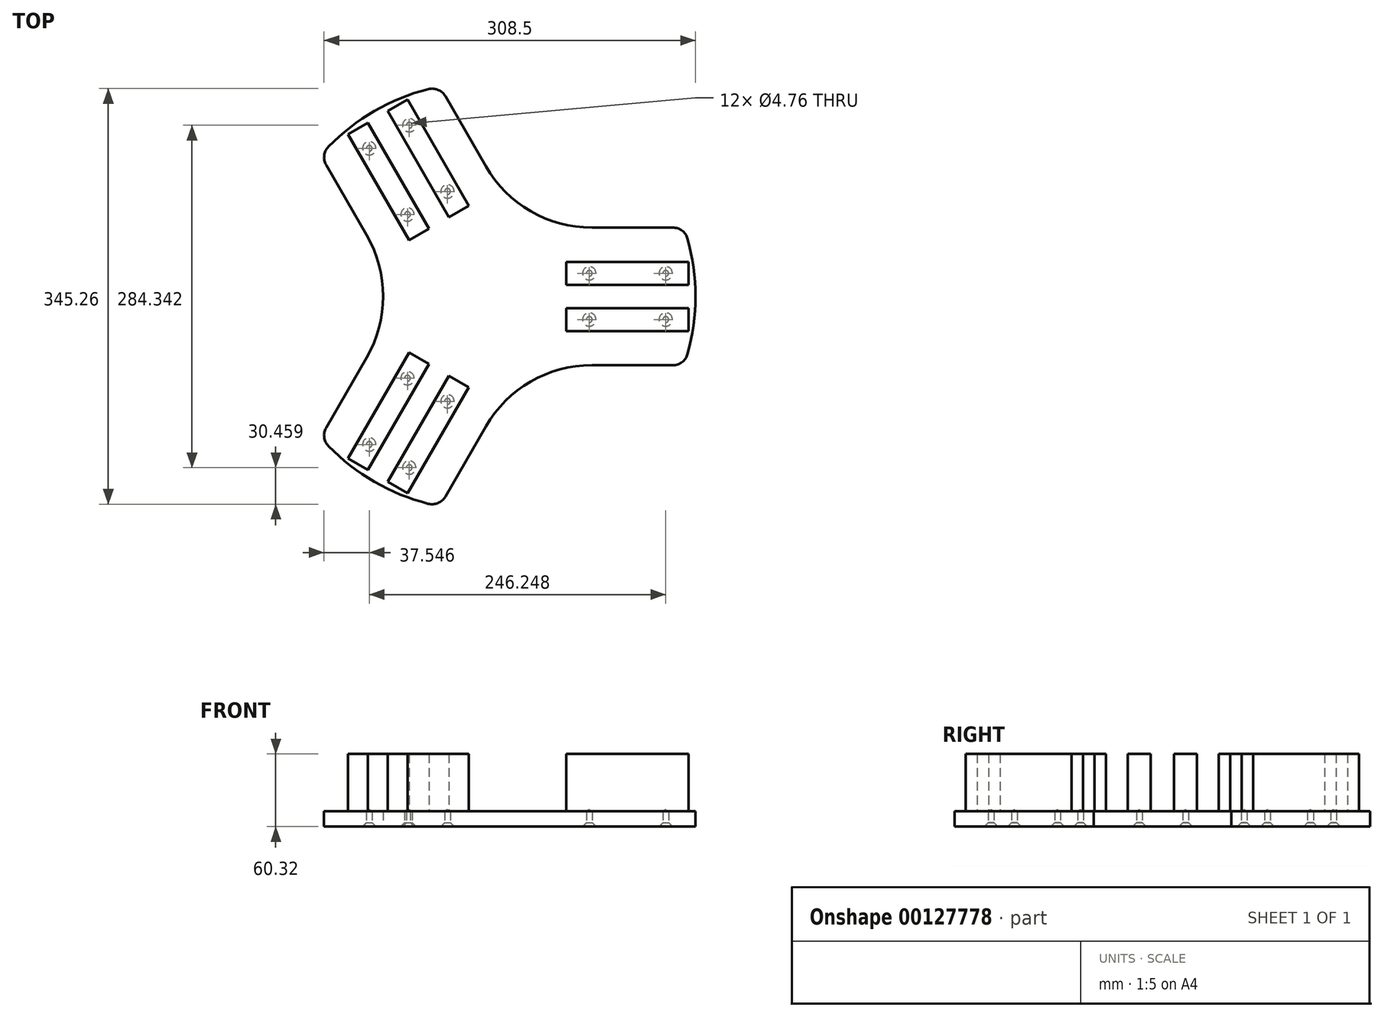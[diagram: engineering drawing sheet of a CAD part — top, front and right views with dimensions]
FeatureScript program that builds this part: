
annotation { "Feature Type Name" : "Feature", "Feature Type Description" : "" }
export const myFeature = defineFeature(function(context is Context, id is Id, definition is map)
    precondition{}
    {
        {
            var Q0;
            Q0=qCreatedBy(makeId("Top.planeOp"),FACE);
            var sketch = newSketch(context, id + "F0", { "sketchPlane" : qUnion([Q0])});
            skArc(sketch, "E0", {"start": v(171.23, -47.87) * mm, "mid": v(177.8, 0) * mm, "end": v(171.23, 47.87) * mm});
            skLineSegment(sketch, "E1", {"start": v(0, 0) * mm, "end": v(177.8, 0) * mm});
            skLineSegment(sketch, "E2", {"start": v(172.14, 9.65) * mm, "end": v(172.14, 28.7) * mm});
            skLineSegment(sketch, "E3.0", {"start": v(70.54, 9.65) * mm, "end": v(70.54, 28.7) * mm});
            skLineSegment(sketch, "E4", {"start": v(70.54, 28.7) * mm, "end": v(172.14, 28.7) * mm});
            skLineSegment(sketch, "E5", {"start": v(172.14, 9.65) * mm, "end": v(70.54, 9.65) * mm});
            skLineSegment(sketch, "E6.MirrorCS", {"start": v(172.14, -9.65) * mm, "end": v(172.14, -28.7) * mm});
            skLineSegment(sketch, "E7.MirrorCS", {"start": v(172.14, -9.65) * mm, "end": v(70.54, -9.65) * mm});
            skLineSegment(sketch, "E8.MirrorCS", {"start": v(70.54, -9.65) * mm, "end": v(70.54, -28.7) * mm});
            skLineSegment(sketch, "E9.MirrorCS", {"start": v(70.54, -28.7) * mm, "end": v(172.14, -28.7) * mm});
            skLineSegment(sketch, "E10.1.0", {"start": v(-60.13, 46.74) * mm, "end": v(-110.93, 134.73) * mm});
            skLineSegment(sketch, "E10.1.1", {"start": v(0, 0) * mm, "end": v(-88.9, 153.98) * mm});
            skLineSegment(sketch, "E10.1.2", {"start": v(-26.91, 65.92) * mm, "end": v(-10.41, 75.44) * mm});
            skLineSegment(sketch, "E10.1.3", {"start": v(-43.63, 56.27) * mm, "end": v(-60.13, 46.74) * mm});
            skLineSegment(sketch, "E10.1.4", {"start": v(-94.43, 144.25) * mm, "end": v(-110.93, 134.73) * mm});
            skLineSegment(sketch, "E10.1.5", {"start": v(-10.41, 75.44) * mm, "end": v(-61.21, 163.43) * mm});
            skLineSegment(sketch, "E10.1.6", {"start": v(-77.71, 153.9) * mm, "end": v(-61.21, 163.43) * mm});
            skLineSegment(sketch, "E10.1.7", {"start": v(-77.71, 153.9) * mm, "end": v(-26.91, 65.92) * mm});
            skLineSegment(sketch, "E10.1.8", {"start": v(-94.43, 144.25) * mm, "end": v(-43.63, 56.27) * mm});
            skLineSegment(sketch, "E10.2.0", {"start": v(-10.41, -75.44) * mm, "end": v(-61.21, -163.43) * mm});
            skLineSegment(sketch, "E10.2.1", {"start": v(0, 0) * mm, "end": v(-88.9, -153.98) * mm});
            skLineSegment(sketch, "E10.2.2", {"start": v(-43.63, -56.27) * mm, "end": v(-60.13, -46.74) * mm});
            skLineSegment(sketch, "E10.2.3", {"start": v(-26.91, -65.92) * mm, "end": v(-10.41, -75.44) * mm});
            skLineSegment(sketch, "E10.2.4", {"start": v(-77.71, -153.9) * mm, "end": v(-61.21, -163.43) * mm});
            skLineSegment(sketch, "E10.2.5", {"start": v(-60.13, -46.74) * mm, "end": v(-110.93, -134.73) * mm});
            skLineSegment(sketch, "E10.2.6", {"start": v(-94.43, -144.25) * mm, "end": v(-110.93, -134.73) * mm});
            skLineSegment(sketch, "E10.2.7", {"start": v(-94.43, -144.25) * mm, "end": v(-43.63, -56.27) * mm});
            skLineSegment(sketch, "E10.2.8", {"start": v(-77.71, -153.9) * mm, "end": v(-26.91, -65.92) * mm});
            skLineSegment(sketch, "E11.0", {"start": v(91.65, -57.15) * mm, "end": v(159, -57.15) * mm});
            skLineSegment(sketch, "E12.0", {"start": v(3.67, -107.95) * mm, "end": v(-30, -166.28) * mm});
            skArc(sketch, "E13.filletArc", {"start": v(91.65, -57.15) * mm, "mid": v(40.85, -70.76) * mm, "end": v(3.67, -107.95) * mm});
            skLineSegment(sketch, "E14.1.0", {"start": v(3.67, 107.95) * mm, "end": v(-30, 166.28) * mm});
            skArc(sketch, "E14.1.1", {"start": v(3.67, 107.95) * mm, "mid": v(40.85, 70.76) * mm, "end": v(91.65, 57.15) * mm});
            skLineSegment(sketch, "E14.1.2", {"start": v(91.65, 57.15) * mm, "end": v(159, 57.15) * mm});
            skLineSegment(sketch, "E14.2.0", {"start": v(-95.32, -50.8) * mm, "end": v(-129, -109.13) * mm});
            skArc(sketch, "E14.2.1", {"start": v(-95.32, -50.8) * mm, "mid": v(-81.7, 0) * mm, "end": v(-95.32, 50.8) * mm});
            skLineSegment(sketch, "E14.2.2", {"start": v(-95.32, 50.8) * mm, "end": v(-129, 109.13) * mm});
            skArc(sketch, "E15.trimOffspring", {"start": v(-44.16, 172.23) * mm, "mid": v(-88.9, 153.98) * mm, "end": v(-127.07, 124.36) * mm});
            skArc(sketch, "E16.trimOffspring", {"start": v(-127.07, -124.36) * mm, "mid": v(-88.9, -153.98) * mm, "end": v(-44.16, -172.23) * mm});
            skPoint(sketch, "E17.visualSharp", {"position": v(-133.68, 117.23) * mm});
            skArc(sketch, "E17.filletArc", {"start": v(-127.07, 124.36) * mm, "mid": v(-130.6, 117.07) * mm, "end": v(-129, 109.13) * mm});
            skPoint(sketch, "E18.visualSharp", {"position": v(-34.69, 174.38) * mm});
            skArc(sketch, "E18.filletArc", {"start": v(-30, 166.28) * mm, "mid": v(-36.08, 171.63) * mm, "end": v(-44.16, 172.23) * mm});
            skPoint(sketch, "E19.visualSharp", {"position": v(168.36, 57.15) * mm});
            skArc(sketch, "E19.filletArc", {"start": v(171.23, 47.87) * mm, "mid": v(166.68, 54.57) * mm, "end": v(159, 57.15) * mm});
            skPoint(sketch, "E20.visualSharp", {"position": v(168.36, -57.15) * mm});
            skArc(sketch, "E20.filletArc", {"start": v(159, -57.15) * mm, "mid": v(166.68, -54.57) * mm, "end": v(171.23, -47.87) * mm});
            skPoint(sketch, "E21.visualSharp", {"position": v(-34.69, -174.38) * mm});
            skArc(sketch, "E21.filletArc", {"start": v(-44.16, -172.23) * mm, "mid": v(-36.08, -171.63) * mm, "end": v(-30, -166.28) * mm});
            skPoint(sketch, "E22.visualSharp", {"position": v(-133.68, -117.23) * mm});
            skArc(sketch, "E22.filletArc", {"start": v(-129, -109.13) * mm, "mid": v(-130.6, -117.07) * mm, "end": v(-127.07, -124.36) * mm});
            skPoint(sketch, "E23", {"position": v(-93.15, -123) * mm});
            skPoint(sketch, "E24", {"position": v(-61.4, -68) * mm});
            skPoint(sketch, "E25", {"position": v(-28.19, -87.18) * mm});
            skPoint(sketch, "E26", {"position": v(-59.94, -142.17) * mm});
            skPoint(sketch, "E27.1.0", {"position": v(153.1, -19.18) * mm});
            skPoint(sketch, "E27.1.1", {"position": v(89.6, -19.18) * mm});
            skPoint(sketch, "E27.1.2", {"position": v(89.6, 19.18) * mm});
            skPoint(sketch, "E27.1.3", {"position": v(153.1, 19.18) * mm});
            skPoint(sketch, "E27.2.0", {"position": v(-59.94, 142.17) * mm});
            skPoint(sketch, "E27.2.1", {"position": v(-28.19, 87.18) * mm});
            skPoint(sketch, "E27.2.2", {"position": v(-61.4, 68) * mm});
            skPoint(sketch, "E27.2.3", {"position": v(-93.15, 123) * mm});
            skSolve(sketch);
        }
        {
            var Q0;
            Q0=makeQuery(id+"F0.imprint","IMPRINT",FACE,{"disambiguationData":[TD([[makeQuery(id+"F0.imprint","IMPRINT",EDGE,{"derivedFrom":sQuery(id+"F0.wireOp",EDGE,"E10.1.0")}),1.0]])]});
            var Q1;
            {var subQ3=sQuery(id+"F0.wireOp",EDGE,"E1");Q1=makeQuery(id+"F0.imprint","IMPRINT",FACE,{"disambiguationData":[TD([[makeQuery(id+"F0.imprint","IMPRINT",EDGE,{"derivedFrom":subQ3}),1.0]])]});}
            var Q2;
            {var subQ2=sQuery(id+"F0.wireOp",EDGE,"E1");Q2=makeQuery(id+"F0.imprint","IMPRINT",FACE,{"disambiguationData":[TD([[makeQuery(id+"F0.imprint","IMPRINT",EDGE,{"derivedFrom":subQ2}),-1.0]])]});}
            extrude(context, id + "F1", {"entities" : qUnion([Q0, Q1, Q2]), "depth" : 12.7 * mm});
        }
        {
            var Q0;
            Q0=makeQuery(id+"F0.imprint","IMPRINT",FACE,{"disambiguationData":[TD([[makeQuery(id+"F0.imprint","IMPRINT",EDGE,{"derivedFrom":sQuery(id+"F0.wireOp",EDGE,"E10.2.2")}),1.0]])]});
            var Q1;
            Q1=makeQuery(id+"F0.imprint","IMPRINT",FACE,{"disambiguationData":[TD([[makeQuery(id+"F0.imprint","IMPRINT",EDGE,{"derivedFrom":sQuery(id+"F0.wireOp",EDGE,"E10.2.0")}),-1.0]])]});
            var Q2;
            Q2=makeQuery(id+"F0.imprint","IMPRINT",FACE,{"disambiguationData":[TD([[makeQuery(id+"F0.imprint","IMPRINT",EDGE,{"derivedFrom":sQuery(id+"F0.wireOp",EDGE,"E6.MirrorCS")}),-1.0]])]});
            var Q3;
            Q3=makeQuery(id+"F0.imprint","IMPRINT",FACE,{"disambiguationData":[TD([[makeQuery(id+"F0.imprint","IMPRINT",EDGE,{"derivedFrom":sQuery(id+"F0.wireOp",EDGE,"E2")}),1.0]])]});
            var Q4;
            Q4=makeQuery(id+"F0.imprint","IMPRINT",FACE,{"disambiguationData":[TD([[makeQuery(id+"F0.imprint","IMPRINT",EDGE,{"derivedFrom":sQuery(id+"F0.wireOp",EDGE,"E10.1.2")}),1.0]])]});
            var Q5;
            Q5=makeQuery(id+"F0.imprint","IMPRINT",FACE,{"disambiguationData":[TD([[makeQuery(id+"F0.imprint","IMPRINT",EDGE,{"derivedFrom":sQuery(id+"F0.wireOp",EDGE,"E10.1.0")}),-1.0]])]});
            extrude(context, id + "F2", {"entities" : qUnion([Q0, Q1, Q2, Q3, Q4, Q5]), "operationType" : NewBodyOperationType.ADD, "depth" : 9.52 * mm});
        }
        {
            var Q0;
            Q0=makeQuery(id+"F2.opExtrude","CAP_FACE",FACE,{"disambiguationData":[OSD([sQuery(id+"F0.wireOp",EDGE,"E10.2.2"),sQuery(id+"F0.wireOp",EDGE,"E10.2.5"),sQuery(id+"F0.wireOp",EDGE,"E10.2.6"),sQuery(id+"F0.wireOp",EDGE,"E10.2.7")])],"isStart":false});
            var Q1;
            Q1=makeQuery(id+"F2.opExtrude","CAP_FACE",FACE,{"disambiguationData":[OSD([sQuery(id+"F0.wireOp",EDGE,"E10.2.0"),sQuery(id+"F0.wireOp",EDGE,"E10.2.3"),sQuery(id+"F0.wireOp",EDGE,"E10.2.4"),sQuery(id+"F0.wireOp",EDGE,"E10.2.8")])],"isStart":false});
            var Q2;
            Q2=makeQuery(id+"F2.opExtrude","CAP_FACE",FACE,{"disambiguationData":[OSD([sQuery(id+"F0.wireOp",EDGE,"E6.MirrorCS"),sQuery(id+"F0.wireOp",EDGE,"E7.MirrorCS"),sQuery(id+"F0.wireOp",EDGE,"E8.MirrorCS"),sQuery(id+"F0.wireOp",EDGE,"E9.MirrorCS")])],"isStart":false});
            var Q3;
            Q3=makeQuery(id+"F2.opExtrude","CAP_FACE",FACE,{"disambiguationData":[OSD([sQuery(id+"F0.wireOp",EDGE,"E2"),sQuery(id+"F0.wireOp",EDGE,"E3.0"),sQuery(id+"F0.wireOp",EDGE,"E4"),sQuery(id+"F0.wireOp",EDGE,"E5")])],"isStart":false});
            var Q4;
            Q4=makeQuery(id+"F2.opExtrude","CAP_FACE",FACE,{"disambiguationData":[OSD([sQuery(id+"F0.wireOp",EDGE,"E10.1.2"),sQuery(id+"F0.wireOp",EDGE,"E10.1.5"),sQuery(id+"F0.wireOp",EDGE,"E10.1.6"),sQuery(id+"F0.wireOp",EDGE,"E10.1.7")])],"isStart":false});
            var Q5;
            Q5=makeQuery(id+"F2.opExtrude","CAP_FACE",FACE,{"disambiguationData":[OSD([sQuery(id+"F0.wireOp",EDGE,"E10.1.0"),sQuery(id+"F0.wireOp",EDGE,"E10.1.3"),sQuery(id+"F0.wireOp",EDGE,"E10.1.4"),sQuery(id+"F0.wireOp",EDGE,"E10.1.8")])],"isStart":false});
            extrude(context, id + "F3", {"entities" : qUnion([Q0, Q1, Q2, Q3, Q4, Q5]), "operationType" : NewBodyOperationType.ADD, "depth" : 50.8 * mm});
        }
        {
            var Q0;
            Q0=sQuery(id+"F0.wireOp",VERTEX,"E23");
            var Q1;
            Q1=sQuery(id+"F0.wireOp",VERTEX,"E26");
            var Q2;
            Q2=sQuery(id+"F0.wireOp",VERTEX,"E25");
            var Q3;
            Q3=sQuery(id+"F0.wireOp",VERTEX,"E24");
            var Q4;
            Q4=sQuery(id+"F0.wireOp",VERTEX,"E27.1.1");
            var Q5;
            Q5=sQuery(id+"F0.wireOp",VERTEX,"E27.1.0");
            var Q6;
            Q6=sQuery(id+"F0.wireOp",VERTEX,"E27.1.3");
            var Q7;
            Q7=sQuery(id+"F0.wireOp",VERTEX,"E27.1.2");
            var Q8;
            Q8=sQuery(id+"F0.wireOp",VERTEX,"E27.2.2");
            var Q9;
            Q9=sQuery(id+"F0.wireOp",VERTEX,"E27.2.1");
            var Q10;
            Q10=sQuery(id+"F0.wireOp",VERTEX,"E27.2.0");
            var Q11;
            Q11=sQuery(id+"F0.wireOp",VERTEX,"E27.2.3");
            var Q12;
            Q12=makeQuery(id+"F1.opExtrude","SWEPT_BODY",BODY,{"disambiguationData":[OSD([sQuery(id+"F0.wireOp",EDGE,"E0"),sQuery(id+"F0.wireOp",EDGE,"E2"),sQuery(id+"F0.wireOp",EDGE,"E3.0"),sQuery(id+"F0.wireOp",EDGE,"E4"),sQuery(id+"F0.wireOp",EDGE,"E5"),sQuery(id+"F0.wireOp",EDGE,"E6.MirrorCS"),sQuery(id+"F0.wireOp",EDGE,"E7.MirrorCS"),sQuery(id+"F0.wireOp",EDGE,"E8.MirrorCS"),sQuery(id+"F0.wireOp",EDGE,"E9.MirrorCS"),sQuery(id+"F0.wireOp",EDGE,"E10.1.0"),sQuery(id+"F0.wireOp",EDGE,"E10.1.2"),sQuery(id+"F0.wireOp",EDGE,"E10.1.3"),sQuery(id+"F0.wireOp",EDGE,"E10.1.4"),sQuery(id+"F0.wireOp",EDGE,"E10.1.5"),sQuery(id+"F0.wireOp",EDGE,"E10.1.6"),sQuery(id+"F0.wireOp",EDGE,"E10.1.7"),sQuery(id+"F0.wireOp",EDGE,"E10.1.8"),sQuery(id+"F0.wireOp",EDGE,"E10.2.0"),sQuery(id+"F0.wireOp",EDGE,"E10.2.2"),sQuery(id+"F0.wireOp",EDGE,"E10.2.3"),sQuery(id+"F0.wireOp",EDGE,"E10.2.4"),sQuery(id+"F0.wireOp",EDGE,"E10.2.5"),sQuery(id+"F0.wireOp",EDGE,"E10.2.6"),sQuery(id+"F0.wireOp",EDGE,"E10.2.7"),sQuery(id+"F0.wireOp",EDGE,"E10.2.8"),sQuery(id+"F0.wireOp",EDGE,"E11.0"),sQuery(id+"F0.wireOp",EDGE,"E12.0"),sQuery(id+"F0.wireOp",EDGE,"E13.filletArc"),sQuery(id+"F0.wireOp",EDGE,"E14.1.0"),sQuery(id+"F0.wireOp",EDGE,"E14.1.1"),sQuery(id+"F0.wireOp",EDGE,"E14.1.2"),sQuery(id+"F0.wireOp",EDGE,"E14.2.0"),sQuery(id+"F0.wireOp",EDGE,"E14.2.1"),sQuery(id+"F0.wireOp",EDGE,"E14.2.2"),sQuery(id+"F0.wireOp",EDGE,"E15.trimOffspring"),sQuery(id+"F0.wireOp",EDGE,"E16.trimOffspring"),sQuery(id+"F0.wireOp",EDGE,"E17.filletArc"),sQuery(id+"F0.wireOp",EDGE,"E18.filletArc"),sQuery(id+"F0.wireOp",EDGE,"E19.filletArc"),sQuery(id+"F0.wireOp",EDGE,"E20.filletArc"),sQuery(id+"F0.wireOp",EDGE,"E21.filletArc"),sQuery(id+"F0.wireOp",EDGE,"E22.filletArc")])]});
            hole(context, id + "F4", {"style" : HoleStyle.C_SINK, "endStyle" : HoleEndStyle.BLIND, "oppositeDirection" : true, "holeDiameter" : 4.76 * mm, "cSinkDiameter" : 11.1 * mm, "cSinkAngle" : 90 * degree, "holeDepth" : 12.7 * mm, "startFromSketch" : true, "locations" : qUnion([Q0, Q1, Q2, Q3, Q4, Q5, Q6, Q7, Q8, Q9, Q10, Q11]), "scope" : qUnion([Q12])});
        }
    });
